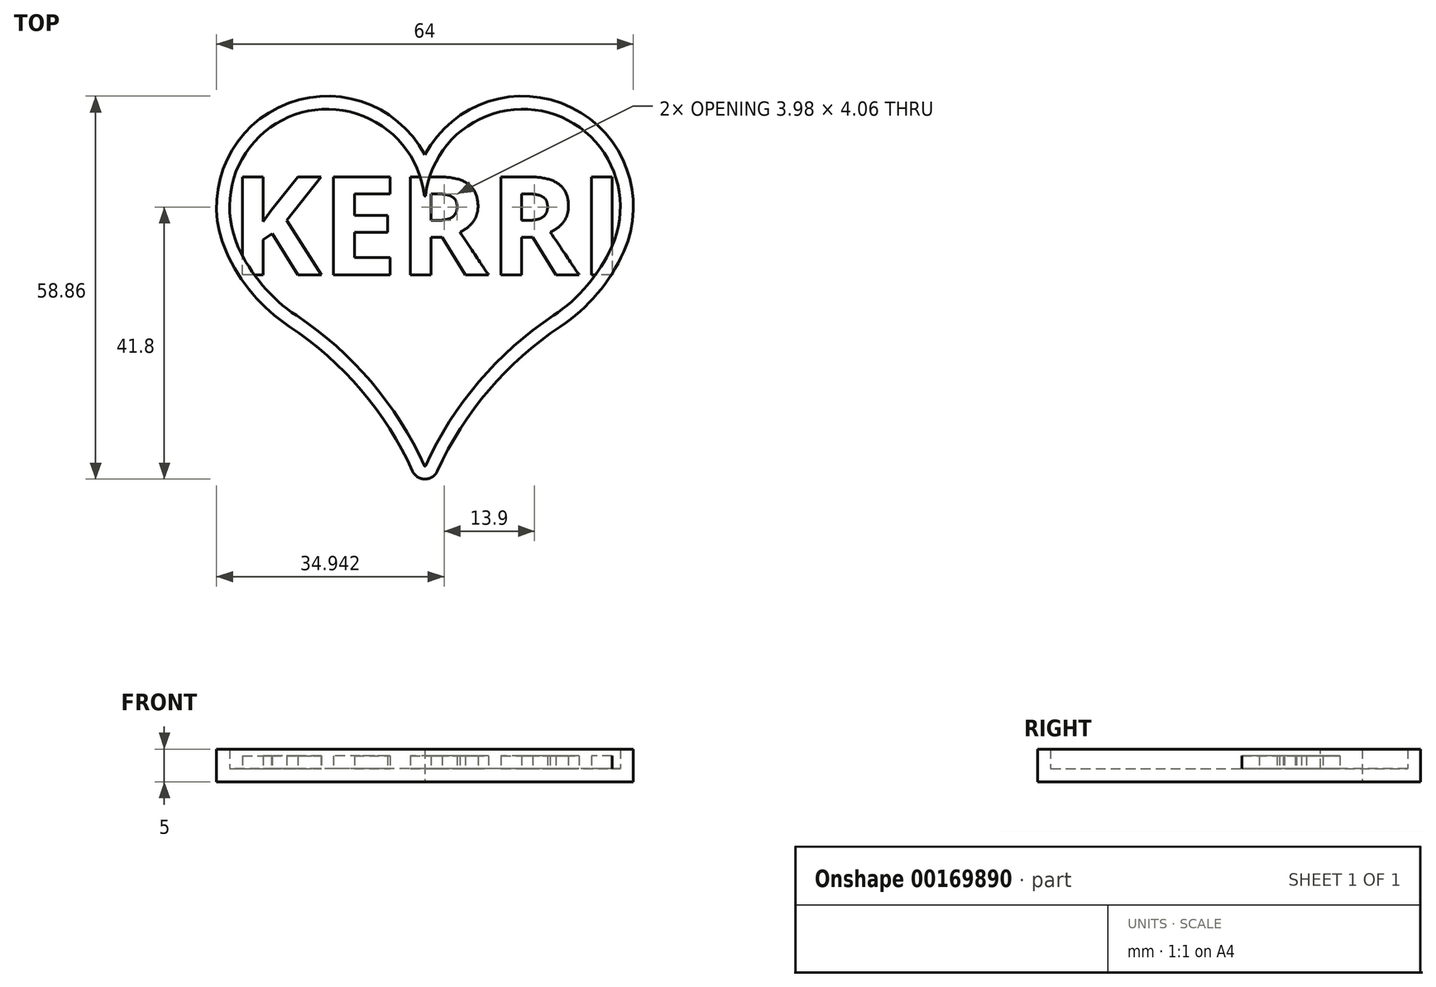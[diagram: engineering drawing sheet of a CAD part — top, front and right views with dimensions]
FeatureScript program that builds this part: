
annotation { "Feature Type Name" : "Feature", "Feature Type Description" : "" }
export const myFeature = defineFeature(function(context is Context, id is Id, definition is map)
    precondition{}
    {
        {
            var Q0;
            Q0=qCreatedBy(makeId("Top.planeOp"),FACE);
            var sketch = newSketch(context, id + "F0", { "sketchPlane" : qUnion([Q0])});
            skArc(sketch, "E0", {"start": v(28.69, 8.87) * mm, "mid": v(18.13, 29.67) * mm, "end": v(0, 15) * mm});
            skArc(sketch, "E1", {"start": v(19.72, -1.73) * mm, "mid": v(24.95, 2.93) * mm, "end": v(28.69, 8.87) * mm});
            skLineSegment(sketch, "E2", {"start": v(15, 15) * mm, "end": v(-15.36, 15) * mm, "construction": true});
            skArc(sketch, "E3", {"start": v(19.72, -1.73) * mm, "mid": v(8.21, -11.97) * mm, "end": v(0, -25) * mm});
            skArc(sketch, "E4.MirrorCS", {"start": v(-28.69, 8.87) * mm, "mid": v(-18.13, 29.67) * mm, "end": v(0, 15) * mm});
            skArc(sketch, "E5.MirrorCS", {"start": v(-19.72, -1.73) * mm, "mid": v(-24.95, 2.93) * mm, "end": v(-28.69, 8.87) * mm});
            skArc(sketch, "E6.MirrorCS", {"start": v(-19.72, -1.73) * mm, "mid": v(-8.21, -11.97) * mm, "end": v(0, -25) * mm});
            skSolve(sketch);
        }
        {
            var Q0;
            Q0=makeQuery(id+"F0.imprint","IMPRINT",FACE,{"disambiguationData":[TD([[makeQuery(id+"F0.imprint","IMPRINT",EDGE,{"derivedFrom":sQuery(id+"F0.wireOp",EDGE,"E0")}),1.0]])]});
            extrude(context, id + "F1", {"entities" : qUnion([Q0]), "depth" : 3 * mm});
        }
        {
            var Q0;
            Q0=makeQuery(id+"F1.opExtrude","SWEPT_EDGE",EDGE,{"disambiguationData":[OSD([sQuery(id+"F0.wireOp",EDGE,"E0"),sQuery(id+"F0.wireOp",EDGE,"E4.MirrorCS")])]});
            var Q1;
            Q1=makeQuery(id+"F1.opExtrude","SWEPT_EDGE",EDGE,{"disambiguationData":[OSD([sQuery(id+"F0.wireOp",EDGE,"E3"),sQuery(id+"F0.wireOp",EDGE,"E6.MirrorCS")])]});
            fillet(context, id + "F2", {"entities" : qUnion([Q0, Q1]), "radius" : .1 * mm, "tangentPropagation" : true, "allowEdgeOverflow" : false});
        }
        {
            var Q0;
            Q0=makeQuery(id+"F1.opExtrude","CAP_FACE",FACE,{"disambiguationData":[OSD([sQuery(id+"F0.wireOp",EDGE,"E0"),sQuery(id+"F0.wireOp",EDGE,"E1"),sQuery(id+"F0.wireOp",EDGE,"E3"),sQuery(id+"F0.wireOp",EDGE,"E4.MirrorCS"),sQuery(id+"F0.wireOp",EDGE,"E5.MirrorCS"),sQuery(id+"F0.wireOp",EDGE,"E6.MirrorCS")])],"isStart":false});
            shell(context, id + "F3", {"entities" : qUnion([Q0]), "thickness" : 2 * mm, "oppositeDirection" : true});
        }
        {
            var Q0;
            Q0=qCreatedBy(makeId("Top.planeOp"),FACE);
            var sketch = newSketch(context, id + "F4", { "sketchPlane" : qUnion([Q0])});
            skText(sketch, "E7", { "text": "KERRI", "fontName": "OpenSans-Bold.ttf"});
            const initialGuessF4  = {"E7": [-0.0299, 0.00455, 1, 0, 0.01516]};
            skSetInitialGuess(sketch, initialGuessF4);
            skSolve(sketch);
        }
        {
            var Q0;
            Q0 = qSketchRegion(id + "F4", true);
            extrude(context, id + "F5", {"entities" : qUnion([Q0]), "depth" : 2 * mm});
        }
    });
